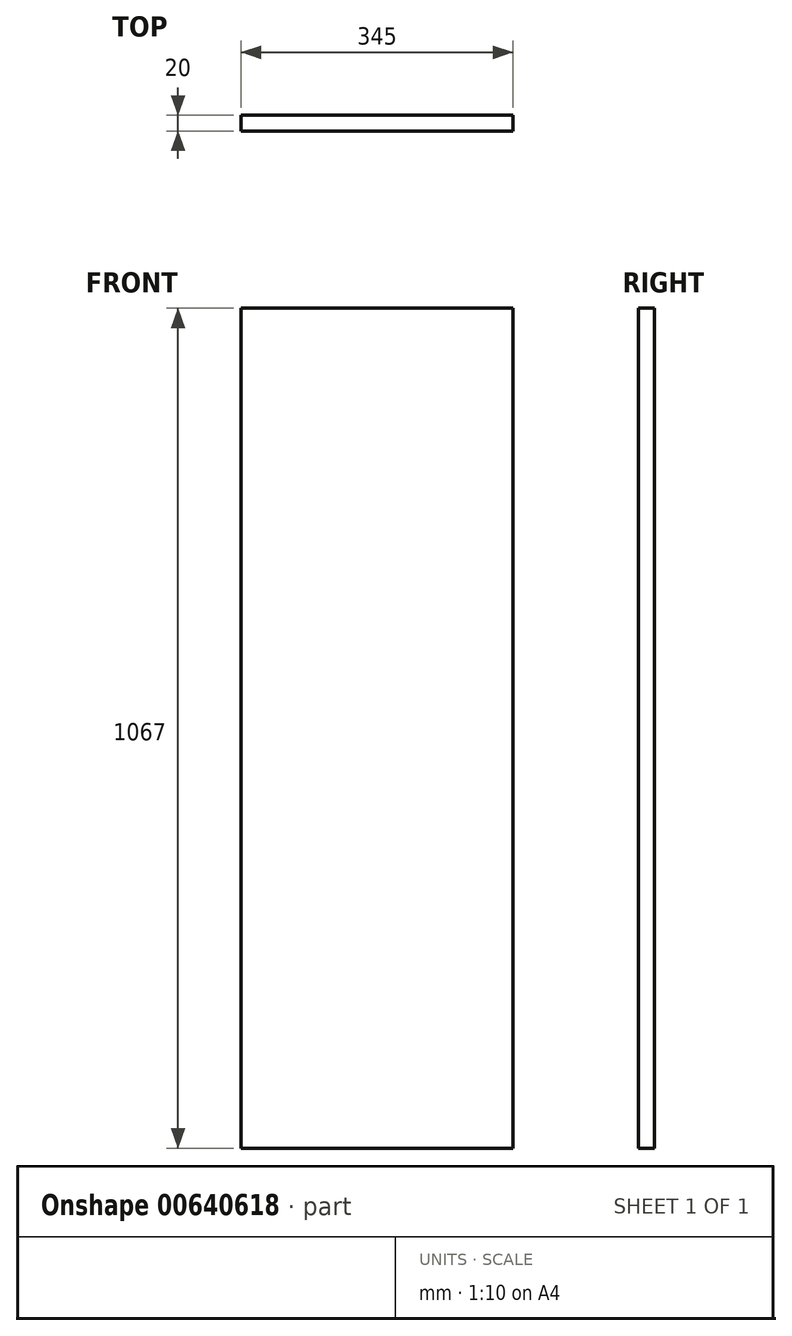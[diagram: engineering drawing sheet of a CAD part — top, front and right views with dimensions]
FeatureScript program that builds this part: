
annotation { "Feature Type Name" : "Feature", "Feature Type Description" : "" }
export const myFeature = defineFeature(function(context is Context, id is Id, definition is map)
    precondition{}
    {
        {
            var Q0;
            Q0=qCreatedBy(makeId("Front.planeOp"),FACE);
            var sketch = newSketch(context, id + "F0", { "sketchPlane" : qUnion([Q0])});
            skLineSegment(sketch, "E0.bottom", {"start": v(0, 0) * mm, "end": v(-345, 0) * mm});
            skLineSegment(sketch, "E0.top", {"start": v(0, 1067) * mm, "end": v(-345, 1067) * mm});
            skLineSegment(sketch, "E0.left", {"start": v(0, 0) * mm, "end": v(0, 1067) * mm});
            skLineSegment(sketch, "E0.right", {"start": v(-345, 0) * mm, "end": v(-345, 1067) * mm});
            skSolve(sketch);
        }
        {
            var Q0;
            Q0 = qSketchRegion(id + "F0", true);
            extrude(context, id + "F1", {"entities" : qUnion([Q0]), "depth" : 20 * mm, "offsetDistance" : 25 * mm});
        }
    });
